# Revit family: VRF_MMD1SPHY_24-27_Indoor Unit
name_source: partatom
category: Mechanical Equipment
revit_build: Autodesk Revit 2017 (Build: 20160225_1515(x64)
units: mm (PartAtom-declared; Revit-internal decimal feet)

## family parameters
Always vertical = Yes
Cut with Voids When Loaded = No
OmniClass Number = 23.75.00.00
OmniClass Title = Climate Control (HVAC)
Part Type = Normal
Room Calculation Point = No
Round Connector Dimension = Use Diameter
Shared = No
Work Plane-Based = No

## types (2) — shared parameters
Article Description = Ducted slim
Capacity = -
Content Supplier URL = www.hcltech.com
Depth (mm) = 450 mm  [stored 1.47638 ft]
Description = Ducted slim
Drain pipe = VP25(OD:32mm)
Duct diameter (mm) = -
EMCS = 4
ETIM Article Class = EC001213
Energy Class = -
Factory default = 10
Frequency (Hz) = 50Hz 220-240V
Height (mm) = 210 mm  [stored 0.688976 ft]
MCA (A) = 0.7
MEPcontent Class = HEATPUMP
MOCP (A) = 15
Manufacturer = Toshiba
Manufacturer URL = https://www.toshiba-carrier.co.jp
Part load = -
Piping diameter (mm)-Gas = 16 mm  [stored 0.0524934 ft]
Piping diameter (mm)-Liquid = 10 mm  [stored 0.0328084 ft]
Power Consumption  W-High = -
Power Consumption  W-Low = -
Power Consumption  W-Mid = -
Product Line = TCAC
Rated efficiency = -
Red = Colour RGB-255 000 000
Refrigerant Information = R410A
Revit Version = 2017
Seasonal & Rated efficiency = -
Sold separetely parts = -
Static pressure (Pa) = 10-20-30-40-50
URL = https://www.toshiba-carrier.co.jp
Voltage (V) = 60Hz 208-230V
Weight (Kg) = 22
White = Colour RGB-255 255 255
Width (mm) = 1100 mm

## per-type parameters (varying)
| type | Airflow (m3/h)- High | Airflow (m3/h)- Low | Airflow (m3/h)- Mid | Capacities kW-Cooling | Capacities kW-Heating | Power consumption-Cooling (Kw) | Power consumption-Heating (Kw) | Running current-Cooling (A) | Running current-Heating (A) | Sound pressure dB(A) - High | Sound pressure dB(A) -Low | Sound pressure dB(A) -Mid | Starting current (A) |
| MMD-UP0241SPHY-E | 1080 | 860 | 950 | 7.1 | 8 | 0.067 | 0.067 | 0.69/ 0.73 | 0.69/ 0.73 | 36 | 31 | 33 | 1.21/ 1.27 |
| MMD-UP0271SPHY-E | 1140 | 910 | 980 | 8 | 9 | 0.072 | 0.072 | 0.74/ 0.78 | 0.74/ 0.78 | 37 | 32 | 34 | 1.30/ 1.36 |

note: column(s) folded — value = type name in every type: Article Type, Manufacturer Art. No., Model

note: [stored X ft] marks values corroborated as IEEE doubles in the binary element streams (Revit-internal decimal feet)

## geometry (parser evidence)
native form markers: Sweep x4
no freeform markers — native parametric forms only
